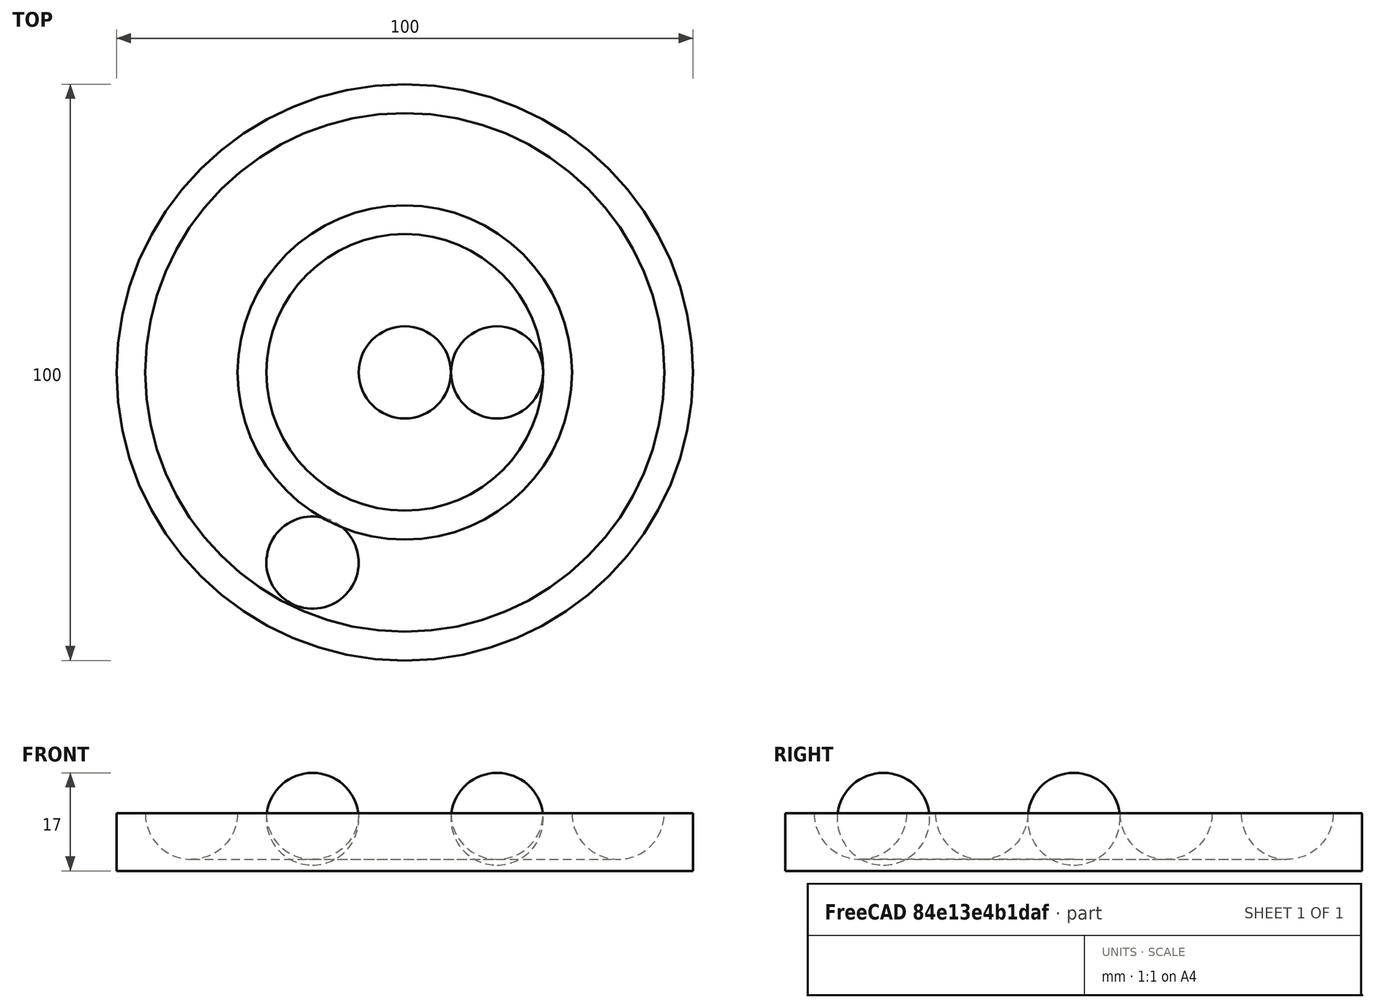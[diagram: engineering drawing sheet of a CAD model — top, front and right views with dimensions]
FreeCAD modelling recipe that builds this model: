
FCSTD DOCUMENT  (FreeCAD 0.21R33771 (Git))
Label: OJT1_T15R02_porta-bales
License: All rights reserved
LicenseURL: http://en.wikipedia.org/wiki/All_rights_reserved
objects: Part::Torus×2, Part::Sphere×2, Part::Cylinder×1, Part::MultiFuse×1, Part::Cut×1
note: 7 computed .brp shape members not serialized (recipe doc carries the construction recipe); baked Part::Feature solids carry a one-line shape summary decoded from their .brp

FEATURE [Part::Cylinder] Cylinder
  Angle = 360
  AttacherType = Attacher::AttachEngine3D
  FirstAngle = 0
  Height = 10
  Radius = 50
  SecondAngle = 0
FEATURE [Part::Torus] Torus
  Angle1 = -180
  Angle2 = 180
  Angle3 = 360
  AttacherType = Attacher::AttachEngine3D
  Placement = pos=(0,0,10) rot=(0,0,1;0rad)
  Radius1 = 16
  Radius2 = 8
FEATURE [Part::Torus] Torus001
  Angle1 = -180
  Angle2 = 180
  Angle3 = 360
  AttacherType = Attacher::AttachEngine3D
  Placement = pos=(0,0,10) rot=(0,0,1;0rad)
  Radius1 = 37
  Radius2 = 8
FEATURE [Part::MultiFuse] Fusion
  Refine = true
  Shapes = -> [Torus001,Torus]
FEATURE [Part::Cut] Cut  label="porta-bales"
  Base = -> Cylinder
  Refine = true
  Tool = -> Fusion
FEATURE [Part::Sphere] Sphere
  Angle1 = -90
  Angle2 = 90
  Angle3 = 360
  AttacherType = Attacher::AttachEngine3D
  Placement = pos=(16,0,9) rot=(0,0,1;0rad)
  Radius = 8
FEATURE [Part::Sphere] Sphere001
  Angle1 = -90
  Angle2 = 90
  Angle3 = 360
  AttacherType = Attacher::AttachEngine3D
  Placement = pos=(-16,-33,9) rot=(0,0,1;0rad)
  Radius = 8
